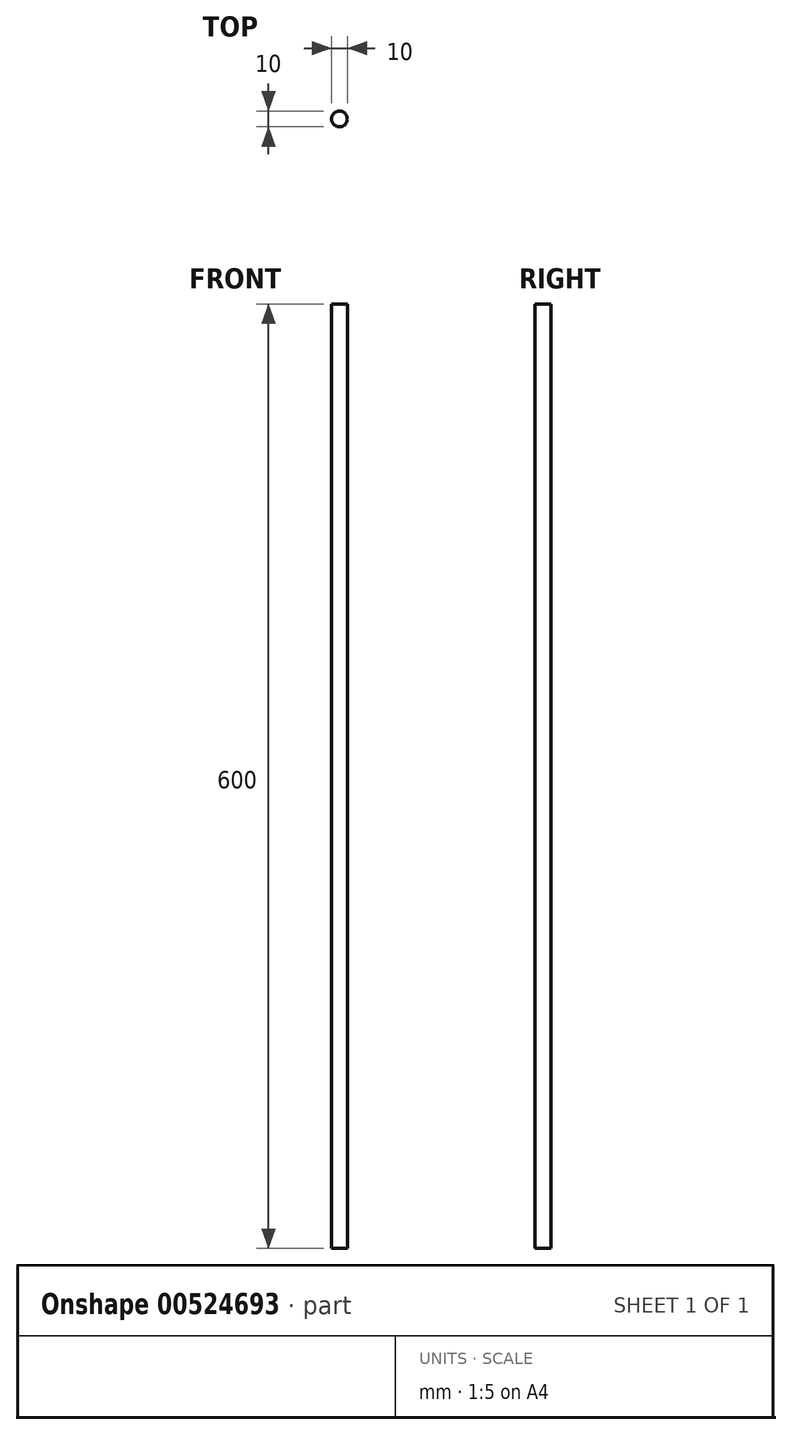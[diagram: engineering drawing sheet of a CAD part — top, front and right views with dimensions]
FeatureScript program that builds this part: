
annotation { "Feature Type Name" : "Feature", "Feature Type Description" : "" }
export const myFeature = defineFeature(function(context is Context, id is Id, definition is map)
    precondition{}
    {
        {
            var Q0;
            Q0=qCreatedBy(makeId("Top.planeOp"),FACE);
            var sketch = newSketch(context, id + "F0", { "sketchPlane" : qUnion([Q0])});
            skCircle(sketch, "E0", {"center": v(-62.47, -46.75) * mm, "radius": 5 * mm});
            skSolve(sketch);
        }
        {
            var Q0;
            Q0=makeQuery(id+"F0.imprint","IMPRINT",FACE,{"disambiguationData":[TD([[makeQuery(id+"F0.imprint","IMPRINT",EDGE,{"derivedFrom":sQuery(id+"F0.wireOp",EDGE,"E0")}),1.0]])]});
            extrude(context, id + "F1", {"entities" : qUnion([Q0]), "depth" : 600 * mm, "offsetDistance" : 25 * mm});
        }
    });
